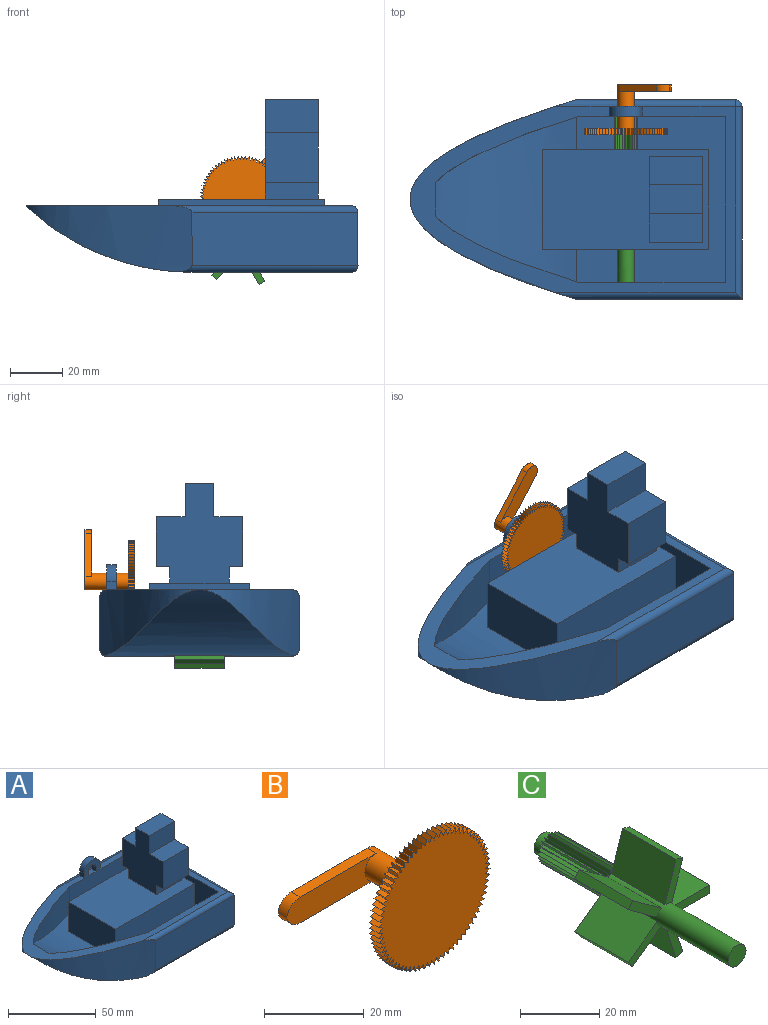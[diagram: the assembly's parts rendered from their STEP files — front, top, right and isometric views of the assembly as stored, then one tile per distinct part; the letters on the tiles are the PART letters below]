
ASSEMBLY  parts=3 mates=2
PART A: 109 faces, bbox 127x76.2x66 mm
  f0: plane 20.32x19.05mm, normal (0,-1,0), area 387.1mm2, adj f2,f4,f103,f105
  f1: plane 20.32x19.05mm, normal (0,1,0), area 387.1mm2, adj f2,f4,f101,f108
  f2: plane 38.1x33.02mm, normal (-1,0,0), area 914mm2, adj f0,f1,f3,f5,f101,f102,f103,f104
  f3: plane 20.32x11.01mm, normal (0,0,1), area 223.7mm2, adj f2,f4,f102,f104
  f4: plane 38.1x33.02mm, normal (1,0,0), area 914mm2, adj f0,f1,f3,f5,f101,f102,f103,f104
  f5: plane 63.5x38.1mm, normal (0,0,1), area 1954.8mm2, adj f2,f4,f6,f49,f50,f51,f106,f107
  f6: plane 63.5x21.59mm, normal (0,1,0), area 1310.3mm2, adj f5,f7,f8,f19,f44,f50,f51
  f7: plane 63.5x57.15mm, normal (0,0,1), area 1412mm2, adj f6,f8,f34,f35,f36,f37,f44,f49
  f8: cylinder r=85.72mm len=62.93mm, axis (0,1,0), area 1923.3mm2, adj f6,f7,f16,f19,f37,f38,f49,f50
  f9: plane 25.4x6.13mm, normal (1,0,0), area 155.7mm2, adj f10,f11,f17,f52
  f10: plane 50.8x6.35mm, normal (0,1,0), area 322.1mm2, adj f9,f17,f18,f39,f52
  f11: plane 50.8x6.35mm, normal (0,-1,0), area 316.7mm2, adj f9,f17,f18,f39,f44,f52
  f12: plane 3.81x3.18mm, normal (-1,0,0), area 12.1mm2, adj f13,f15,f36,f48
  f13: cylinder r=3.17mm len=6.35mm, axis (0,1,0), area 38mm2, adj f12,f14,f36,f48
  f14: plane 3.81x3.18mm, normal (1,0,0), area 12.1mm2, adj f13,f15,f36,f48
  f15: plane 6.35x3.81mm, normal (0,0,1), area 24.2mm2, adj f12,f14,f27,f36
  f16: plane 124.46x76.2mm, normal (0,0,1), area 1581.7mm2, adj f8,f23,f24,f25,f26,f27,f34,f35
  f17: cylinder r=92.08mm len=72.89mm, axis (0,1,0), area 3266.8mm2, adj f9,f10,f11,f18,f23,f24,f30,f31
  f18: plane 71.12x60.96mm, normal (0,0,-1), area 3206.4mm2, adj f10,f11,f17,f30,f31,f33,f39
  f19: plane 15.94x12.7mm, normal (0,0,1), area 202.3mm2, adj f6,f8,f36,f38,f44
  f20: plane 73.66x20.32mm, normal (1,0,0), area 1496.8mm2, adj f21,f26,f29,f33
  f21: plane 63.5x20.32mm, normal (0,-1,0), area 1290.3mm2, adj f20,f23,f25,f31
  f22: plane 60.96x20.32mm, normal (0,1,0), area 1238.7mm2, adj f24,f27,f29,f30
  f23: extruded ~63.5x38.1mm, area 1205.2mm2, adj f16,f17,f21,f25,f31
  f24: extruded ~63.5x38.1mm, area 1205.2mm2, adj f16,f17,f22,f27,f30
  f25: cylinder r=2.54mm len=71.68mm, axis (1,0,0), area 261.7mm2, adj f16,f21,f23,f26
  f26: cylinder r=2.54mm len=73.66mm, axis (0,1,0), area 290.2mm2, adj f16,f20,f25,f28
  f27: cylinder r=2.54mm len=69.14mm, axis (-1,0,0), area 255.2mm2, adj f15,f16,f22,f24,f28,f48
  f28: sphere r=2.54mm, area 10.1mm2, adj f26,f27,f29
  f29: cylinder r=2.54mm len=20.32mm, axis (0,0,1), area 81.1mm2, adj f20,f22,f28,f32
  f30: cylinder r=2.54mm len=66.36mm, axis (1,0,0), area 251.6mm2, adj f17,f18,f22,f24,f32
  f31: cylinder r=2.54mm len=68.9mm, axis (-1,0,0), area 258mm2, adj f17,f18,f21,f23,f33
  f32: sphere r=2.54mm, area 10.1mm2, adj f29,f30,f33
  f33: cylinder r=2.54mm len=73.66mm, axis (0,1,0), area 290.2mm2, adj f18,f20,f31,f32
  f34: plane 63.5x19.05mm, normal (-1,0,0), area 1209.7mm2, adj f7,f16,f35,f36
  f35: plane 56.22x19.05mm, normal (0,1,0), area 1039.2mm2, adj f7,f16,f34,f37,f42
  f36: plane 56.22x29.85mm, normal (0,-1,0), area 1112.3mm2, adj f7,f12,f13,f14,f15,f16,f19,f34
  f37: extruded ~54.82x25.42mm, area 775.8mm2, adj f7,f8,f16,f35
  f38: extruded ~54.82x25.42mm, area 775.8mm2, adj f8,f16,f19,f36
  f39: plane 25.4x6.35mm, normal (-1,0,0), area 161.3mm2, adj f10,f11,f18,f52
  f40: plane 6.35x6.35mm, normal (0,-1,0), area 31.7mm2, adj f41
  f41: cylinder r=3.17mm len=6.35mm, axis (0,-1,0), area 50.7mm2, adj f36,f40
  f42: cylinder r=3.17mm len=6.35mm, axis (0,-1,0), area 63.3mm2, adj f35,f43
  f43: plane 6.35x6.35mm, normal (0,1,0), area 31.7mm2, adj f42
  f44: cylinder r=4.45mm len=19.05mm, axis (0,-1,0), area 158mm2, adj f6,f7,f11,f19,f36,f52,f97
  f45: plane 3.81x3.18mm, normal (-1,0,0), area 12.1mm2, adj f16,f36,f46,f48
  f46: cylinder r=6.35mm len=12.7mm, axis (0,1,0), area 76mm2, adj f36,f45,f47,f48
  f47: plane 3.81x3.18mm, normal (1,0,0), area 12.1mm2, adj f16,f36,f46,f48
  f48: plane 12.7x9.53mm, normal (0,1,0), area 67.7mm2, adj f12,f13,f14,f27,f45,f46,f47
  f49: plane 63.5x21.59mm, normal (0,-1,0), area 1335.3mm2, adj f5,f7,f8,f50,f51,f100
  f50: plane 38.1x20.64mm, normal (-1,0,0), area 786.5mm2, adj f5,f6,f8,f49
  f51: plane 38.1x21.59mm, normal (1,0,0), area 822.6mm2, adj f5,f6,f7,f49
  f52: plane 53.34x31.75mm, normal (0,0,1), area 204.6mm2, adj f9,f10,f11,f39,f44,f55,f56,f57
  f53: plane 66.04x58.42mm, normal (0,0,-1), area 1751.6mm2, adj f54,f80,f81,f82,f83,f90,f95,f97
  f54: cylinder r=87mm len=65.59mm, axis (0,1,0), area 2170.5mm2, adj f53,f62,f65,f83,f84,f95,f96,f97
  f55: plane 27.94x4.76mm, normal (-1,0,0), area 133mm2, adj f52,f56,f57,f63
  f56: plane 53.34x5.08mm, normal (0,-1,0), area 270.2mm2, adj f52,f55,f63,f64,f85
  f57: plane 53.34x5.08mm, normal (0,1,0), area 253.2mm2, adj f52,f55,f63,f64,f85,f90
  f58: plane 4.45x1.27mm, normal (1,0,0), area 5.6mm2, adj f59,f61,f82,f94
  f59: cylinder r=4.45mm len=8.89mm, axis (0,1,0), area 17.7mm2, adj f58,f60,f82,f94
  f60: plane 4.45x1.27mm, normal (-1,0,0), area 5.6mm2, adj f59,f61,f82,f94
  f61: plane 8.89x1.27mm, normal (0,0,-1), area 11.3mm2, adj f58,f60,f82,f94
  f62: plane 121.21x69.86mm, normal (0,0,-1), area 949.6mm2, adj f54,f63,f69,f70,f71,f72,f80,f81
  f63: cylinder r=90.8mm len=71.8mm, axis (0,1,0), area 2991.2mm2, adj f55,f56,f57,f62,f64,f69,f70,f76
  f64: plane 71.12x60.96mm, normal (0,0,1), area 3058.1mm2, adj f56,f57,f63,f76,f77,f79,f85
  f65: plane 15.46x15.24mm, normal (0,0,-1), area 235.5mm2, adj f54,f82,f84,f90,f97
  f66: plane 72.39x20.32mm, normal (-1,0,0), area 1471mm2, adj f67,f72,f75,f79
  f67: plane 62.04x20.32mm, normal (0,1,0), area 1260.7mm2, adj f66,f69,f71,f77
  f68: plane 60.77x20.32mm, normal (0,-1,0), area 1234.9mm2, adj f70,f73,f75,f76
  f69: extruded ~60.43x30.44mm, area 1027.6mm2, adj f62,f63,f67,f71,f77
  f70: extruded ~60.43x30.44mm, area 1026.5mm2, adj f62,f63,f68,f73,f76,f94
  f71: cylinder r=1.27mm len=66.2mm, axis (1,0,0), area 125.9mm2, adj f62,f67,f69,f72
  f72: cylinder r=1.27mm len=72.39mm, axis (0,1,0), area 144.4mm2, adj f62,f66,f71,f73,f74,f94
  f73: cylinder r=1.27mm len=68.95mm, axis (-1,0,0), area 257.3mm2, adj f68,f70,f72,f74,f94
  f74: sphere r=1.27mm, area 2.5mm2, adj f72,f73,f75
  f75: cylinder r=1.27mm len=20.32mm, axis (0,0,1), area 40.5mm2, adj f66,f68,f74,f78
  f76: cylinder r=1.27mm len=63.84mm, axis (1,0,0), area 123.6mm2, adj f63,f64,f68,f70,f78
  f77: cylinder r=1.27mm len=65.11mm, axis (-1,0,0), area 125.2mm2, adj f63,f64,f67,f69,f79
  f78: sphere r=1.27mm, area 2.5mm2, adj f75,f76,f79
  f79: cylinder r=1.27mm len=72.39mm, axis (0,1,0), area 143.5mm2, adj f64,f66,f77,f78
  f80: plane 66.04x19.05mm, normal (1,0,0), area 1258.1mm2, adj f53,f62,f81,f82
  f81: plane 57.67x19.05mm, normal (0,-1,0), area 1036.6mm2, adj f53,f62,f80,f83,f88
  f82: plane 57.67x29.85mm, normal (0,1,0), area 1058mm2, adj f53,f58,f59,f60,f61,f62,f65,f80
  f83: extruded ~55.08x25.32mm, area 777.4mm2, adj f53,f54,f62,f81
  f84: extruded ~55.08x25.32mm, area 777.4mm2, adj f54,f62,f65,f82
  f85: plane 27.94x5.08mm, normal (1,0,0), area 141.9mm2, adj f52,f56,f57,f64
  f86: plane 8.89x8.89mm, normal (0,1,0), area 62.1mm2, adj f87
  f87: cylinder r=4.45mm len=8.89mm, axis (0,-1,0), area 70.9mm2, adj f82,f86
  f88: cylinder r=4.45mm len=8.89mm, axis (0,-1,0), area 88.7mm2, adj f81,f89
  f89: plane 8.89x8.89mm, normal (0,-1,0), area 62.1mm2, adj f88
  f90: cylinder r=5.71mm len=19.05mm, axis (0,-1,0), area 161.1mm2, adj f52,f53,f57,f65,f82,f97
  f91: plane 4.45x1.27mm, normal (1,0,0), area 5.6mm2, adj f62,f82,f92,f94
  f92: cylinder r=5.08mm len=10.16mm, axis (0,1,0), area 20.3mm2, adj f82,f91,f93,f94
  f93: plane 4.45x1.27mm, normal (-1,0,0), area 5.6mm2, adj f62,f82,f92,f94
  f94: plane 68.95x10.8mm, normal (0,-1,0), area 101.4mm2, adj f58,f59,f60,f61,f62,f70,f72,f73
  f95: plane 60.96x21.59mm, normal (0,1,0), area 1281.6mm2, adj f53,f54,f96,f98,f99,f100
  f96: plane 35.56x20.84mm, normal (1,0,0), area 740.9mm2, adj f54,f95,f97,f99
  f97: plane 60.96x21.59mm, normal (0,-1,0), area 1245.9mm2, adj f44,f52,f53,f54,f65,f90,f96,f98
  f98: plane 35.56x21.59mm, normal (-1,0,0), area 767.7mm2, adj f53,f95,f97,f99
  f99: plane 60.96x35.56mm, normal (0,0,-1), area 2167.7mm2, adj f95,f96,f97,f98
  f100: cylinder r=3.17mm len=6.35mm, axis (0,1,0), area 25.3mm2, adj f49,f95
  f101: plane 20.32x11.01mm, normal (0,0,1), area 223.7mm2, adj f1,f2,f4,f102
  f102: plane 20.32x12.7mm, normal (0,1,0), area 258.1mm2, adj f2,f3,f4,f101
  f103: plane 20.32x11.01mm, normal (0,0,1), area 223.7mm2, adj f0,f2,f4,f104
  f104: plane 20.32x12.7mm, normal (0,-1,0), area 258.1mm2, adj f2,f3,f4,f103
  f105: plane 20.32x5.08mm, normal (0,0,-1), area 103.2mm2, adj f0,f2,f4,f106
  f106: plane 20.32x6.35mm, normal (0,-1,0), area 129mm2, adj f2,f4,f5,f105
  f107: plane 20.32x6.35mm, normal (0,1,0), area 129mm2, adj f2,f4,f5,f108
  f108: plane 20.32x5.08mm, normal (0,0,-1), area 103.2mm2, adj f1,f2,f4,f107
PART B: 155 faces, bbox 41.2x19.1x31.7 mm
  f0: cylinder r=3.17mm len=16.51mm, axis (0,-1,0), area 304mm2, adj f1,f148,f150,f151,f152
  f1: plane 28.52x6.35mm, normal (0,1,0), area 170.9mm2, adj f0,f150,f151,f153,f154
  f2: plane 2.54x1.22mm, normal (-0.89,0,-0.46), area 3.5mm2, adj f3,f147,f148,f149
  f3: plane 2.54x1.22mm, normal (0.89,0,-0.46), area 3.5mm2, adj f2,f4,f148,f149
  f4: plane 2.54x1.16mm, normal (-0.84,0,-0.53), area 3.5mm2, adj f3,f5,f148,f149
  f5: plane 2.54x1.27mm, normal (0.92,0,-0.38), area 3.5mm2, adj f4,f6,f148,f149
  f6: plane 2.54x1.09mm, normal (-0.8,0,-0.61), area 3.5mm2, adj f5,f7,f148,f149
  f7: plane 2.54x1.31mm, normal (0.95,0,-0.3), area 3.5mm2, adj f6,f8,f148,f149
  f8: plane 2.54x1.02mm, normal (-0.74,0,-0.67), area 3.5mm2, adj f7,f9,f148,f149
  f9: plane 2.54x1.34mm, normal (0.98,0,-0.22), area 3.5mm2, adj f8,f10,f148,f149
  f10: plane 2.54x1.01mm, normal (-0.68,0,-0.73), area 3.5mm2, adj f9,f11,f148,f149
  f11: plane 2.54x1.36mm, normal (0.99,0,-0.13), area 3.5mm2, adj f10,f12,f148,f149
  f12: plane 2.54x1.08mm, normal (-0.61,0,-0.79), area 3.5mm2, adj f11,f13,f148,f149
  f13: plane 2.54x1.37mm, normal (1,0,-0.05), area 3.5mm2, adj f12,f14,f148,f149
  f14: plane 2.54x1.15mm, normal (-0.54,0,-0.84), area 3.5mm2, adj f13,f15,f148,f149
  f15: plane 2.54x1.37mm, normal (1,0,0.04), area 3.5mm2, adj f14,f16,f148,f149
  f16: plane 2.54x1.21mm, normal (-0.47,0,-0.88), area 3.5mm2, adj f15,f17,f148,f149
  f17: plane 2.54x1.36mm, normal (0.99,0,0.12), area 3.5mm2, adj f16,f18,f148,f149
  f18: plane 2.54x1.26mm, normal (-0.39,0,-0.92), area 3.5mm2, adj f17,f19,f148,f149
  f19: plane 2.54x1.34mm, normal (0.98,0,0.21), area 3.5mm2, adj f18,f20,f148,f149
  f20: plane 2.54x1.3mm, normal (-0.31,0,-0.95), area 3.5mm2, adj f19,f21,f148,f149
  f21: plane 2.54x1.31mm, normal (0.96,0,0.29), area 3.5mm2, adj f20,f22,f148,f149
  f22: plane 2.54x1.33mm, normal (-0.23,0,-0.97), area 3.5mm2, adj f21,f23,f148,f149
  f23: plane 2.54x1.27mm, normal (0.93,0,0.37), area 3.5mm2, adj f22,f24,f148,f149
  f24: plane 2.54x1.36mm, normal (-0.15,0,-0.99), area 3.5mm2, adj f23,f25,f148,f149
  f25: plane 2.54x1.22mm, normal (0.89,0,0.45), area 3.5mm2, adj f24,f26,f148,f149
  f26: plane 2.54x1.37mm, normal (-0.06,0,-1), area 3.5mm2, adj f25,f27,f148,f149
  f27: plane 2.54x1.17mm, normal (0.85,0,0.53), area 3.5mm2, adj f26,f28,f148,f149
  f28: plane 2.54x1.37mm, normal (0.03,0,-1), area 3.5mm2, adj f27,f29,f148,f149
  f29: plane 2.54x1.1mm, normal (0.8,0,0.6), area 3.5mm2, adj f28,f30,f148,f149
  f30: plane 2.54x1.36mm, normal (0.11,0,-0.99), area 3.5mm2, adj f29,f31,f148,f149
  f31: plane 2.54x1.02mm, normal (0.75,0,0.66), area 3.5mm2, adj f30,f32,f148,f149
  f32: plane 2.54x1.34mm, normal (0.2,0,-0.98), area 3.5mm2, adj f31,f33,f148,f149
  f33: plane 2.54x1mm, normal (0.69,0,0.73), area 3.5mm2, adj f32,f34,f148,f149
  f34: plane 2.54x1.32mm, normal (0.28,0,-0.96), area 3.5mm2, adj f33,f35,f148,f149
  f35: plane 2.54x1.07mm, normal (0.62,0,0.78), area 3.5mm2, adj f34,f36,f148,f149
  f36: plane 2.54x1.28mm, normal (0.36,0,-0.93), area 3.5mm2, adj f35,f37,f148,f149
  f37: plane 2.54x1.14mm, normal (0.55,0,0.83), area 3.5mm2, adj f36,f38,f148,f149
  f38: plane 2.54x1.23mm, normal (0.44,0,-0.9), area 3.5mm2, adj f37,f39,f148,f149
  f39: plane 2.54x1.2mm, normal (0.48,0,0.88), area 3.5mm2, adj f38,f40,f148,f149
  f40: plane 2.54x1.17mm, normal (0.52,0,-0.86), area 3.5mm2, adj f39,f41,f148,f149
  f41: plane 2.54x1.26mm, normal (0.4,0,0.92), area 3.5mm2, adj f40,f42,f148,f149
  f42: plane 2.54x1.11mm, normal (0.59,0,-0.81), area 3.5mm2, adj f41,f43,f148,f149
  f43: plane 2.54x1.3mm, normal (0.32,0,0.95), area 3.5mm2, adj f42,f44,f148,f149
  f44: plane 2.54x1.04mm, normal (0.66,0,-0.76), area 3.5mm2, adj f43,f45,f148,f149
  f45: plane 2.54x1.33mm, normal (0.24,0,0.97), area 3.5mm2, adj f44,f46,f148,f149
  f46: plane 2.54x0.98mm, normal (0.72,0,-0.7), area 3.5mm2, adj f45,f47,f148,f149
  f47: plane 2.54x1.35mm, normal (0.16,0,0.99), area 3.5mm2, adj f46,f48,f148,f149
  f48: plane 2.54x1.06mm, normal (0.78,0,-0.63), area 3.5mm2, adj f47,f49,f148,f149
  f49: plane 2.54x1.37mm, normal (0.07,0,1), area 3.5mm2, adj f48,f50,f148,f149
  f50: plane 2.54x1.13mm, normal (0.83,0,-0.56), area 3.5mm2, adj f49,f51,f148,f149
  f51: plane 2.54x1.37mm, normal (-0.02,0,1), area 3.5mm2, adj f50,f52,f148,f149
  f52: plane 2.54x1.2mm, normal (0.87,0,-0.49), area 3.5mm2, adj f51,f53,f148,f149
  f53: plane 2.54x1.36mm, normal (-0.1,0,0.99), area 3.5mm2, adj f52,f54,f148,f149
  f54: plane 2.54x1.25mm, normal (0.91,0,-0.41), area 3.5mm2, adj f53,f55,f148,f149
  f55: plane 2.54x1.35mm, normal (-0.19,0,0.98), area 3.5mm2, adj f54,f56,f148,f149
  f56: plane 2.54x1.29mm, normal (0.94,0,-0.33), area 3.5mm2, adj f55,f57,f148,f149
  f57: plane 2.54x1.32mm, normal (-0.27,0,0.96), area 3.5mm2, adj f56,f58,f148,f149
  f58: plane 2.54x1.33mm, normal (0.97,0,-0.25), area 3.5mm2, adj f57,f59,f148,f149
  f59: plane 2.54x1.28mm, normal (-0.35,0,0.94), area 3.5mm2, adj f58,f60,f148,f149
  f60: plane 2.54x1.35mm, normal (0.99,0,-0.17), area 3.5mm2, adj f59,f61,f148,f149
  f61: plane 2.54x1.24mm, normal (-0.43,0,0.9), area 3.5mm2, adj f60,f62,f148,f149
  f62: plane 2.54x1.37mm, normal (1,0,-0.08), area 3.5mm2, adj f61,f63,f148,f149
  f63: plane 2.54x1.18mm, normal (-0.51,0,0.86), area 3.5mm2, adj f62,f64,f148,f149
  f64: plane 2.54x1.37mm, normal (1,0,0.01), area 3.5mm2, adj f63,f65,f148,f149
  f65: plane 2.54x1.12mm, normal (-0.58,0,0.81), area 3.5mm2, adj f64,f66,f148,f149
  f66: plane 2.54x1.37mm, normal (1,0,0.09), area 3.5mm2, adj f65,f67,f148,f149
  f67: plane 2.54x1.04mm, normal (-0.65,0,0.76), area 3.5mm2, adj f66,f68,f148,f149
  f68: plane 2.54x1.35mm, normal (0.98,0,0.18), area 3.5mm2, adj f67,f69,f148,f149
  f69: plane 2.54x0.98mm, normal (-0.71,0,0.7), area 3.5mm2, adj f68,f70,f148,f149
  f70: plane 2.54x1.32mm, normal (0.97,0,0.26), area 3.5mm2, adj f69,f71,f148,f149
  f71: plane 2.54x1.05mm, normal (-0.77,0,0.64), area 3.5mm2, adj f70,f72,f148,f149
  f72: plane 2.54x1.29mm, normal (0.94,0,0.34), area 3.5mm2, adj f71,f73,f148,f149
  f73: plane 2.54x1.13mm, normal (-0.82,0,0.57), area 3.5mm2, adj f72,f74,f148,f149
  f74: plane 2.54x1.24mm, normal (0.91,0,0.42), area 3.5mm2, adj f73,f75,f148,f149
  f75: plane 2.54x1.19mm, normal (-0.87,0,0.5), area 3.5mm2, adj f74,f76,f148,f149
  f76: plane 2.54x1.19mm, normal (0.87,0,0.5), area 3.5mm2, adj f75,f77,f148,f149
  f77: plane 2.54x1.24mm, normal (-0.91,0,0.42), area 3.5mm2, adj f76,f78,f148,f149
  f78: plane 2.54x1.13mm, normal (0.82,0,0.57), area 3.5mm2, adj f77,f79,f148,f149
  f79: plane 2.54x1.29mm, normal (-0.94,0,0.34), area 3.5mm2, adj f78,f80,f148,f149
  f80: plane 2.54x1.05mm, normal (0.77,0,0.64), area 3.5mm2, adj f79,f81,f148,f149
  f81: plane 2.54x1.32mm, normal (-0.97,0,0.26), area 3.5mm2, adj f80,f82,f148,f149
  f82: plane 2.54x0.98mm, normal (0.71,0,0.7), area 3.5mm2, adj f81,f83,f148,f149
  f83: plane 2.54x1.35mm, normal (-0.98,0,0.18), area 3.5mm2, adj f82,f84,f148,f149
  f84: plane 2.54x1.04mm, normal (0.65,0,0.76), area 3.5mm2, adj f83,f85,f148,f149
  f85: plane 2.54x1.37mm, normal (-1,0,0.09), area 3.5mm2, adj f84,f86,f148,f149
  f86: plane 2.54x1.12mm, normal (0.58,0,0.81), area 3.5mm2, adj f85,f87,f148,f149
  f87: plane 2.54x1.37mm, normal (-1,0,0.01), area 3.5mm2, adj f86,f88,f148,f149
  f88: plane 2.54x1.18mm, normal (0.51,0,0.86), area 3.5mm2, adj f87,f89,f148,f149
  f89: plane 2.54x1.37mm, normal (-1,0,-0.08), area 3.5mm2, adj f88,f90,f148,f149
  f90: plane 2.54x1.24mm, normal (0.43,0,0.9), area 3.5mm2, adj f89,f91,f148,f149
  f91: plane 2.54x1.35mm, normal (-0.99,0,-0.17), area 3.5mm2, adj f90,f92,f148,f149
  f92: plane 2.54x1.28mm, normal (0.35,0,0.94), area 3.5mm2, adj f91,f93,f148,f149
  f93: plane 2.54x1.33mm, normal (-0.97,0,-0.25), area 3.5mm2, adj f92,f94,f148,f149
  f94: plane 2.54x1.32mm, normal (0.27,0,0.96), area 3.5mm2, adj f93,f95,f148,f149
  f95: plane 2.54x1.29mm, normal (-0.94,0,-0.33), area 3.5mm2, adj f94,f96,f148,f149
  f96: plane 2.54x1.35mm, normal (0.19,0,0.98), area 3.5mm2, adj f95,f97,f148,f149
  f97: plane 2.54x1.25mm, normal (-0.91,0,-0.41), area 3.5mm2, adj f96,f98,f148,f149
  f98: plane 2.54x1.36mm, normal (0.1,0,0.99), area 3.5mm2, adj f97,f99,f148,f149
  f99: plane 2.54x1.2mm, normal (-0.87,0,-0.49), area 3.5mm2, adj f98,f100,f148,f149
  f100: plane 2.54x1.37mm, normal (0.02,0,1), area 3.5mm2, adj f99,f101,f148,f149
  f101: plane 2.54x1.13mm, normal (-0.83,0,-0.56), area 3.5mm2, adj f100,f102,f148,f149
  f102: plane 2.54x1.37mm, normal (-0.07,0,1), area 3.5mm2, adj f101,f103,f148,f149
  f103: plane 2.54x1.06mm, normal (-0.78,0,-0.63), area 3.5mm2, adj f102,f104,f148,f149
  f104: plane 2.54x1.35mm, normal (-0.16,0,0.99), area 3.5mm2, adj f103,f105,f148,f149
  f105: plane 2.54x0.98mm, normal (-0.72,0,-0.7), area 3.5mm2, adj f104,f106,f148,f149
  f106: plane 2.54x1.33mm, normal (-0.24,0,0.97), area 3.5mm2, adj f105,f107,f148,f149
  f107: plane 2.54x1.04mm, normal (-0.66,0,-0.76), area 3.5mm2, adj f106,f108,f148,f149
  f108: plane 2.54x1.3mm, normal (-0.32,0,0.95), area 3.5mm2, adj f107,f109,f148,f149
  f109: plane 2.54x1.11mm, normal (-0.59,0,-0.81), area 3.5mm2, adj f108,f110,f148,f149
  f110: plane 2.54x1.26mm, normal (-0.4,0,0.92), area 3.5mm2, adj f109,f111,f148,f149
  f111: plane 2.54x1.17mm, normal (-0.52,0,-0.86), area 3.5mm2, adj f110,f112,f148,f149
  f112: plane 2.54x1.2mm, normal (-0.48,0,0.88), area 3.5mm2, adj f111,f113,f148,f149
  f113: plane 2.54x1.23mm, normal (-0.44,0,-0.9), area 3.5mm2, adj f112,f114,f148,f149
  f114: plane 2.54x1.14mm, normal (-0.55,0,0.83), area 3.5mm2, adj f113,f115,f148,f149
  f115: plane 2.54x1.28mm, normal (-0.36,0,-0.93), area 3.5mm2, adj f114,f116,f148,f149
  f116: plane 2.54x1.07mm, normal (-0.62,0,0.78), area 3.5mm2, adj f115,f117,f148,f149
  f117: plane 2.54x1.32mm, normal (-0.28,0,-0.96), area 3.5mm2, adj f116,f118,f148,f149
  f118: plane 2.54x1mm, normal (-0.69,0,0.73), area 3.5mm2, adj f117,f119,f148,f149
  f119: plane 2.54x1.34mm, normal (-0.2,0,-0.98), area 3.5mm2, adj f118,f120,f148,f149
  f120: plane 2.54x1.02mm, normal (-0.75,0,0.66), area 3.5mm2, adj f119,f121,f148,f149
  f121: plane 2.54x1.36mm, normal (-0.11,0,-0.99), area 3.5mm2, adj f120,f122,f148,f149
  f122: plane 2.54x1.1mm, normal (-0.8,0,0.6), area 3.5mm2, adj f121,f123,f148,f149
  f123: plane 2.54x1.37mm, normal (-0.03,0,-1), area 3.5mm2, adj f122,f124,f148,f149
  f124: plane 2.54x1.17mm, normal (-0.85,0,0.53), area 3.5mm2, adj f123,f125,f148,f149
  f125: plane 2.54x1.37mm, normal (0.06,0,-1), area 3.5mm2, adj f124,f126,f148,f149
  f126: plane 2.54x1.22mm, normal (-0.89,0,0.45), area 3.5mm2, adj f125,f127,f148,f149
  f127: plane 2.54x1.36mm, normal (0.15,0,-0.99), area 3.5mm2, adj f126,f128,f148,f149
  f128: plane 2.54x1.27mm, normal (-0.93,0,0.37), area 3.5mm2, adj f127,f129,f148,f149
  f129: plane 2.54x1.33mm, normal (0.23,0,-0.97), area 3.5mm2, adj f128,f130,f148,f149
  f130: plane 2.54x1.31mm, normal (-0.96,0,0.29), area 3.5mm2, adj f129,f131,f148,f149
  f131: plane 2.54x1.3mm, normal (0.31,0,-0.95), area 3.5mm2, adj f130,f132,f148,f149
  f132: plane 2.54x1.34mm, normal (-0.98,0,0.21), area 3.5mm2, adj f131,f133,f148,f149
  f133: plane 2.54x1.26mm, normal (0.39,0,-0.92), area 3.5mm2, adj f132,f134,f148,f149
  f134: plane 2.54x1.36mm, normal (-0.99,0,0.12), area 3.5mm2, adj f133,f135,f148,f149
  f135: plane 2.54x1.21mm, normal (0.47,0,-0.88), area 3.5mm2, adj f134,f136,f148,f149
  f136: plane 2.54x1.37mm, normal (-1,0,0.04), area 3.5mm2, adj f135,f137,f148,f149
  f137: plane 2.54x1.15mm, normal (0.54,0,-0.84), area 3.5mm2, adj f136,f138,f148,f149
  f138: plane 2.54x1.37mm, normal (-1,0,-0.05), area 3.5mm2, adj f137,f139,f148,f149
  f139: plane 2.54x1.08mm, normal (0.61,0,-0.79), area 3.5mm2, adj f138,f140,f148,f149
  f140: plane 2.54x1.36mm, normal (-0.99,0,-0.13), area 3.5mm2, adj f139,f141,f148,f149
  f141: plane 2.54x1.01mm, normal (0.68,0,-0.73), area 3.5mm2, adj f140,f142,f148,f149
  f142: plane 2.54x1.34mm, normal (-0.98,0,-0.22), area 3.5mm2, adj f141,f143,f148,f149
  f143: plane 2.54x1.02mm, normal (0.74,0,-0.67), area 3.5mm2, adj f142,f144,f148,f149
  f144: plane 2.54x1.31mm, normal (-0.95,0,-0.3), area 3.5mm2, adj f143,f145,f148,f149
  f145: plane 2.54x1.09mm, normal (0.8,0,-0.61), area 3.5mm2, adj f144,f146,f148,f149
  f146: plane 2.54x1.27mm, normal (-0.92,0,-0.38), area 3.5mm2, adj f145,f147,f148,f149
  f147: plane 2.54x1.16mm, normal (0.84,0,-0.53), area 3.5mm2, adj f2,f146,f148,f149
  f148: plane 31.74x31.74mm, normal (0,1,0), area 699.8mm2, adj f0,f2,f3,f4,f5,f6,f7,f8
  f149: plane 31.74x31.74mm, normal (0,-1,0), area 731.5mm2, adj f2,f3,f4,f5,f6,f7,f8,f9
  f150: plane 21.59x2.54mm, normal (0,0,1), area 54.8mm2, adj f0,f1,f152,f153
  f151: plane 21.59x2.54mm, normal (0,0,-1), area 54.8mm2, adj f0,f1,f152,f154
  f152: plane 25.35x6.35mm, normal (0,-1,0), area 139.2mm2, adj f0,f150,f151,f153,f154
  f153: cylinder r=3.81mm len=3.76mm, axis (0,1,0), area 13.6mm2, adj f1,f150,f152,f154
  f154: cylinder r=3.81mm len=3.76mm, axis (0,1,0), area 13.6mm2, adj f1,f151,f152,f153
PART C: 108 faces, bbox 29x69.2x30.5 mm
  f0: plane 12.57x6.22mm, normal (0,1,0), area 30.5mm2, adj f16,f17,f18,f82,f83,f84,f85,f86
  f1: plane 11.66x8.93mm, normal (0,1,0), area 30.4mm2, adj f12,f13,f14,f74,f75,f76,f77,f78
  f2: plane 11.66x8.93mm, normal (0,1,0), area 30.4mm2, adj f9,f10,f11,f64,f65,f66,f67,f68
  f3: plane 12.57x6.22mm, normal (0,1,0), area 30.5mm2, adj f8,f22,f23,f100,f101,f102,f103,f104
  f4: plane 12.86x6.34mm, normal (0,-1,0), area 31.8mm2, adj f15,f16,f17,f18
  f5: plane 11.77x9.52mm, normal (0,-1,0), area 31.8mm2, adj f12,f13,f14,f15
  f6: plane 11.77x9.52mm, normal (0,-1,0), area 31.8mm2, adj f9,f10,f11,f15
  f7: plane 12.86x6.34mm, normal (0,-1,0), area 31.8mm2, adj f8,f15,f22,f23
  f8: plane 19.05x12.08mm, normal (-0.95,0,0.31), area 241.9mm2, adj f3,f7,f15,f23,f51
  f9: plane 19.05x10.27mm, normal (0.59,0,0.81), area 241.9mm2, adj f2,f6,f10,f15,f52
  f10: plane 19.05x2.06mm, normal (-0.81,0,0.59), area 48.4mm2, adj f2,f6,f9,f11
  f11: plane 19.05x10.27mm, normal (-0.59,0,-0.81), area 241.9mm2, adj f2,f6,f10,f15,f53
  f12: plane 19.05x10.27mm, normal (-0.59,0,0.81), area 241.9mm2, adj f1,f5,f13,f15,f55
  f13: plane 19.05x2.06mm, normal (-0.81,0,-0.59), area 48.4mm2, adj f1,f5,f12,f14
  f14: plane 19.05x10.27mm, normal (0.59,0,-0.81), area 241.9mm2, adj f1,f5,f13,f15,f56
  f15: cylinder r=3.17mm len=44.45mm, axis (0,1,0), area 637.8mm2, adj f4,f5,f6,f7,f8,f9,f11,f12
  f16: plane 19.05x12.08mm, normal (-0.95,0,-0.31), area 241.9mm2, adj f0,f4,f15,f17,f57
  f17: plane 19.05x2.42mm, normal (0.31,0,-0.95), area 48.4mm2, adj f0,f4,f16,f18
  f18: plane 19.05x12.08mm, normal (0.95,0,0.31), area 241.9mm2, adj f0,f4,f15,f17,f58
  f19: plane 19.05x12.7mm, normal (0,0,-1), area 241.9mm2, adj f15,f20,f24,f25,f60
  f20: plane 19.05x2.54mm, normal (1,0,0), area 48.4mm2, adj f19,f21,f24,f25
  f21: plane 19.05x12.7mm, normal (0,0,1), area 241.9mm2, adj f15,f20,f24,f25,f48
  f22: plane 19.05x12.08mm, normal (0.95,0,-0.31), area 241.9mm2, adj f3,f7,f15,f23,f50
  f23: plane 19.05x2.42mm, normal (0.31,0,0.95), area 48.4mm2, adj f3,f7,f8,f22
  f24: plane 12.7x2.54mm, normal (0,-1,0), area 31.8mm2, adj f15,f19,f20,f21
  f25: plane 12.47x2.54mm, normal (0,1,0), area 30.2mm2, adj f19,f20,f21,f91,f92,f93,f94,f95
  f26: plane 6.35x6.35mm, normal (0,-1,0), area 31.7mm2, adj f15
  f27: plane 1.35x0.89mm, normal (0,1,0), area 0.6mm2, adj f83,f84,f107
  f28: plane 1.37x0.95mm, normal (0,1,0), area 0.6mm2, adj f85,f86,f107
  f29: plane 1.28x1.19mm, normal (0,1,0), area 0.6mm2, adj f87,f88,f107
  f30: plane 1.33x1.08mm, normal (0,1,0), area 0.6mm2, adj f89,f90,f107
  f31: plane 1.37x0.87mm, normal (0,1,0), area 0.6mm2, adj f91,f92,f107
  f32: plane 1.3x0.9mm, normal (0,1,0), area 0.6mm2, adj f93,f94,f107
  f33: plane 1.37x0.87mm, normal (0,1,0), area 0.6mm2, adj f95,f96,f107
  f34: plane 1.33x1.08mm, normal (0,1,0), area 0.6mm2, adj f97,f98,f107
  f35: plane 1.28x1.19mm, normal (0,1,0), area 0.6mm2, adj f99,f100,f107
  f36: plane 1.37x0.95mm, normal (0,1,0), area 0.6mm2, adj f101,f102,f107
  f37: plane 1.35x0.89mm, normal (0,1,0), area 0.6mm2, adj f103,f104,f107
  f38: plane 1.35x0.89mm, normal (0,1,0), area 0.6mm2, adj f62,f105,f107
  f39: plane 1.37x0.95mm, normal (0,1,0), area 0.6mm2, adj f63,f64,f107
  f40: plane 1.28x1.19mm, normal (0,1,0), area 0.6mm2, adj f65,f66,f107
  f41: plane 1.33x1.08mm, normal (0,1,0), area 0.6mm2, adj f67,f68,f107
  f42: plane 1.37x0.87mm, normal (0,1,0), area 0.6mm2, adj f69,f70,f107
  f43: plane 1.3x0.9mm, normal (0,1,0), area 0.6mm2, adj f71,f72,f107
  f44: plane 1.37x0.87mm, normal (0,1,0), area 0.6mm2, adj f73,f74,f107
  f45: plane 1.33x1.08mm, normal (0,1,0), area 0.6mm2, adj f75,f76,f107
  f46: plane 1.28x1.19mm, normal (0,1,0), area 0.6mm2, adj f77,f78,f107
  f47: plane 1.37x0.95mm, normal (0,1,0), area 0.6mm2, adj f79,f80,f107
  f48: plane 0.98x0.05mm, normal (0,-1,0), area 0mm2, adj f15,f21,f96
  f49: plane 1.33x1.08mm, normal (0,-1,0), area 0.6mm2, adj f15,f97,f98
  f50: plane 1.28x0.8mm, normal (0,-1,0), area 0.4mm2, adj f15,f22,f99,f100
  f51: plane 1.35x0.71mm, normal (0,-1,0), area 0.5mm2, adj f8,f15,f62,f105
  f52: plane 1.3x0.95mm, normal (0,-1,0), area 0.6mm2, adj f9,f15,f63,f64
  f53: plane 1.16x0.82mm, normal (0,-1,0), area 0.3mm2, adj f11,f15,f69,f70
  f54: plane 1.3x0.9mm, normal (0,-1,0), area 0.6mm2, adj f15,f71,f72
  f55: plane 1.16x0.82mm, normal (0,-1,0), area 0.3mm2, adj f12,f15,f73,f74
  f56: plane 1.3x0.95mm, normal (0,-1,0), area 0.6mm2, adj f14,f15,f79,f80
  f57: plane 1.35x0.71mm, normal (0,-1,0), area 0.5mm2, adj f15,f16,f81,f82
  f58: plane 1.28x0.8mm, normal (0,-1,0), area 0.4mm2, adj f15,f18,f87,f88
  f59: plane 1.33x1.08mm, normal (0,-1,0), area 0.6mm2, adj f15,f89,f90
  f60: plane 0.98x0.05mm, normal (0,-1,0), area 0mm2, adj f15,f19,f91
  f61: plane 1.35x0.89mm, normal (0,1,0), area 0.6mm2, adj f81,f82,f107
  f62: plane 22.23x1.35mm, normal (-0.98,0,0.19), area 30.5mm2, adj f38,f51,f63,f105
  f63: plane 22.23x0.99mm, normal (0.72,0,0.69), area 30.5mm2, adj f39,f52,f62,f64
  f64: plane 22.23x1.37mm, normal (-1,0,-0.09), area 30.5mm2, adj f2,f39,f52,f63,f65
  f65: plane 22.23x1.19mm, normal (0.5,0,0.87), area 30.5mm2, adj f2,f40,f64,f66
  f66: plane 22.23x1.28mm, normal (-0.93,0,-0.37), area 30.5mm2, adj f2,f40,f65,f67
  f67: plane 22.23x1.33mm, normal (0.23,0,0.97), area 30.5mm2, adj f2,f41,f66,f68
  f68: plane 22.23x1.08mm, normal (-0.79,0,-0.62), area 30.5mm2, adj f2,f41,f67,f69
  f69: plane 22.23x1.37mm, normal (-0.05,0,1), area 30.5mm2, adj f2,f42,f53,f68,f70
  f70: plane 22.23x1.12mm, normal (-0.58,0,-0.81), area 30.5mm2, adj f42,f53,f69,f71
  f71: plane 22.23x1.3mm, normal (-0.33,0,0.94), area 30.5mm2, adj f43,f54,f70,f72
  f72: plane 22.23x1.3mm, normal (-0.33,0,-0.94), area 30.5mm2, adj f43,f54,f71,f73
  f73: plane 22.23x1.12mm, normal (-0.58,0,0.81), area 30.5mm2, adj f44,f55,f72,f74
  f74: plane 22.23x1.37mm, normal (-0.05,0,-1), area 30.5mm2, adj f1,f44,f55,f73,f75
  f75: plane 22.23x1.08mm, normal (-0.79,0,0.62), area 30.5mm2, adj f1,f45,f74,f76
  f76: plane 22.23x1.33mm, normal (0.23,0,-0.97), area 30.5mm2, adj f1,f45,f75,f77
  f77: plane 22.23x1.28mm, normal (-0.93,0,0.37), area 30.5mm2, adj f1,f46,f76,f78
  f78: plane 22.23x1.19mm, normal (0.5,0,-0.87), area 30.5mm2, adj f1,f46,f77,f79
  f79: plane 22.23x1.37mm, normal (-1,0,0.09), area 30.5mm2, adj f1,f47,f56,f78,f80
  f80: plane 22.23x0.99mm, normal (0.72,0,-0.69), area 30.5mm2, adj f47,f56,f79,f81
  f81: plane 22.23x1.35mm, normal (-0.98,0,-0.19), area 30.5mm2, adj f57,f61,f80,f82
  f82: plane 22.23x1.22mm, normal (0.89,0,-0.46), area 30.5mm2, adj f0,f57,f61,f81,f83
  f83: plane 22.23x1.22mm, normal (-0.89,0,-0.46), area 30.5mm2, adj f0,f27,f82,f84
  f84: plane 22.23x1.35mm, normal (0.98,0,-0.19), area 30.5mm2, adj f0,f27,f83,f85
  f85: plane 22.23x0.99mm, normal (-0.72,0,-0.69), area 30.5mm2, adj f0,f28,f84,f86
  f86: plane 22.23x1.37mm, normal (1,0,0.09), area 30.5mm2, adj f0,f28,f85,f87
  f87: plane 22.23x1.19mm, normal (-0.5,0,-0.87), area 30.5mm2, adj f0,f29,f58,f86,f88
  f88: plane 22.23x1.28mm, normal (0.93,0,0.37), area 30.5mm2, adj f29,f58,f87,f89
  f89: plane 22.23x1.33mm, normal (-0.23,0,-0.97), area 30.5mm2, adj f30,f59,f88,f90
  f90: plane 22.23x1.08mm, normal (0.79,0,0.62), area 30.5mm2, adj f30,f59,f89,f91
  f91: plane 22.23x1.37mm, normal (0.05,0,-1), area 30.5mm2, adj f25,f31,f60,f90,f92
  f92: plane 22.23x1.12mm, normal (0.58,0,0.81), area 30.5mm2, adj f25,f31,f91,f93
  f93: plane 22.23x1.3mm, normal (0.33,0,-0.94), area 30.5mm2, adj f25,f32,f92,f94
  f94: plane 22.23x1.3mm, normal (0.33,0,0.94), area 30.5mm2, adj f25,f32,f93,f95
  f95: plane 22.23x1.12mm, normal (0.58,0,-0.81), area 30.5mm2, adj f25,f33,f94,f96
  f96: plane 22.23x1.37mm, normal (0.05,0,1), area 30.5mm2, adj f25,f33,f48,f95,f97
  f97: plane 22.23x1.08mm, normal (0.79,0,-0.62), area 30.5mm2, adj f34,f49,f96,f98
  f98: plane 22.23x1.33mm, normal (-0.23,0,0.97), area 30.5mm2, adj f34,f49,f97,f99
  f99: plane 22.23x1.28mm, normal (0.93,0,-0.37), area 30.5mm2, adj f35,f50,f98,f100
  f100: plane 22.23x1.19mm, normal (-0.5,0,0.87), area 30.5mm2, adj f3,f35,f50,f99,f101
  f101: plane 22.23x1.37mm, normal (1,0,-0.09), area 30.5mm2, adj f3,f36,f100,f102
  f102: plane 22.23x0.99mm, normal (-0.72,0,0.69), area 30.5mm2, adj f3,f36,f101,f103
  f103: plane 22.23x1.35mm, normal (0.98,0,0.19), area 30.5mm2, adj f3,f37,f102,f104
  f104: plane 22.23x1.22mm, normal (-0.89,0,0.46), area 30.5mm2, adj f3,f37,f103,f105
  f105: plane 22.23x1.22mm, normal (0.89,0,0.46), area 30.5mm2, adj f3,f38,f51,f62,f104
  f106: plane 6.35x6.35mm, normal (0,1,0), area 31.7mm2, adj f107
  f107: cylinder r=3.17mm len=6.35mm, axis (0,1,0), area 50.7mm2, adj f27,f28,f29,f30,f31,f32,f33,f34
PLACE A t=(71.75,82.48,-7.04)mm fixed
PLACE B rot(axis=(0,1,0),130.9deg) t=(100.86,81.84,12.62)mm
PLACE C rot(axis=(0,-1,0),155.6deg) t=(101.58,82.48,-45.25)mm
MATE revolute B.f0 <-> A.f13  axis (0,-1,0) through (90.8,79.94,-3.87)mm
MATE revolute C.f15 <-> A.f41  axis (0,1,0) through (90.8,78.67,-22.92)mm
